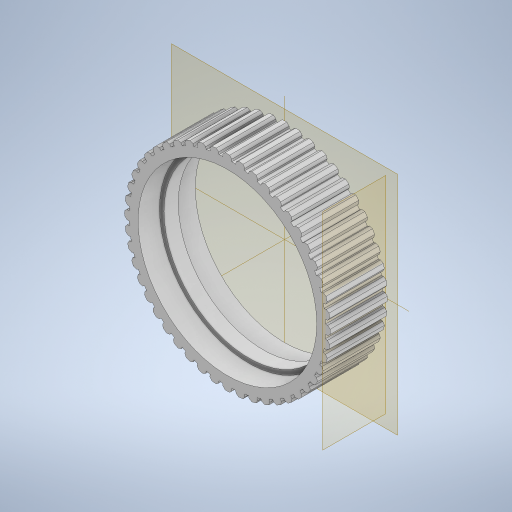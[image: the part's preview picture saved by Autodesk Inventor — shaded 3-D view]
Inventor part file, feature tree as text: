
AUTODESK INVENTOR PART (.ipt)
format: ipt  version: 2024 (Build 280153000, 153)  size: 550,400 bytes
history: native  units: in
note: dims shown in document units (in); Inventor stores cm internally (conversion verified against a paired STEP export)
features: sketch x3, extrude x2, revolve x1, plane x1, chamfer x1, pattern_circular x1
ambient origin geometry x8: Origin, YZ Plane, XZ Plane, XY Plane, X Axis, Y Axis, Z Axis, Center Point
bodies: Solid1 (feature_tree)
feature tree (9):
  extrude  "Extrusion1"  Depth=2.75in
  revolve  "Revolution1"  [1 undecoded]
  plane  "Work Plane1"
  extrude  "Extrusion2"  Depth=0.125in
  chamfer  "Chamfer1"  Distance=0.2in
  pattern_circular  "Circular Pattern2"  Angle=90.0deg  [1 undecoded]
  sketch  "Sketch1"  dims[d0=2.5in d1=2.75in]
  sketch  "Sketch2"  dims[d2=0.8in d3=0.0in d5=0.3in]
  sketch  "Sketch3"  dims[d6=0.3in d7=0.0625in d8=0.2in d9=90.0deg d20=0.0625in d21=0.0in d26=0.125in d27=0.0312in d28=0.125in d29=45.0deg d30=18.8976in d31=360.0deg]
note: 2 required parameter values undecoded (feature->parameter linkage not recoverable at this tier; creation-order binding heuristic only, values carry confidence <= 0.55)